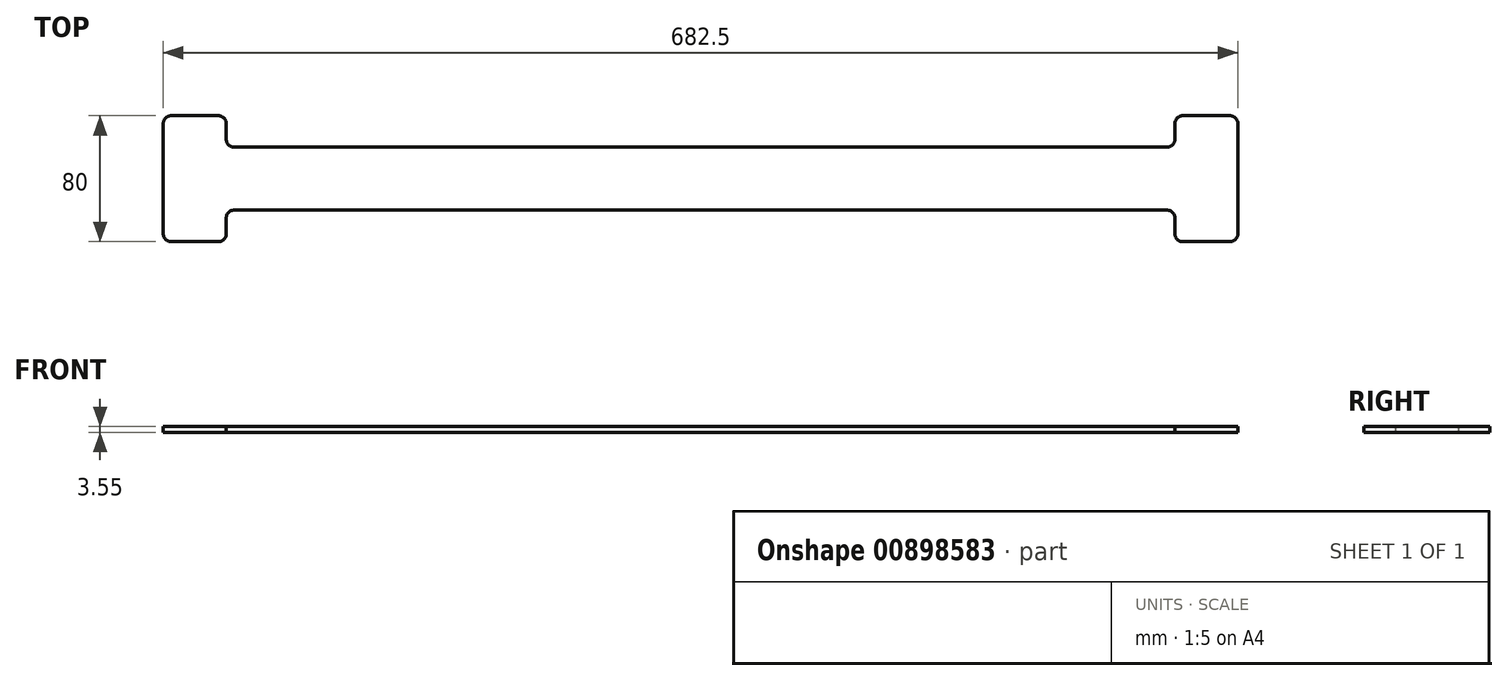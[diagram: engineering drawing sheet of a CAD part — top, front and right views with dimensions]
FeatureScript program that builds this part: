
annotation { "Feature Type Name" : "Feature", "Feature Type Description" : "" }
export const myFeature = defineFeature(function(context is Context, id is Id, definition is map)
    precondition{}
    {
        {
            var Q0;
            Q0=qCreatedBy(makeId("Top.planeOp"),FACE);
            var sketch = newSketch(context, id + "F0", { "sketchPlane" : qUnion([Q0])});
            skLineSegment(sketch, "E0.bottom", {"start": v(341.25, 20) * mm, "end": v(-341.25, 20) * mm});
            skLineSegment(sketch, "E0.top", {"start": v(341.25, -20) * mm, "end": v(-341.25, -20) * mm});
            skLineSegment(sketch, "E0.left", {"start": v(341.25, 20) * mm, "end": v(341.25, -20) * mm});
            skLineSegment(sketch, "E0.right", {"start": v(-341.25, 20) * mm, "end": v(-341.25, -20) * mm});
            skPoint(sketch, "E0.middle", {"position": v(0, 0) * mm});
            skLineSegment(sketch, "E1.bottom", {"start": v(-341.25, 0) * mm, "end": v(-301.25, 0) * mm, "construction": true});
            skLineSegment(sketch, "E1.top", {"start": v(-341.25, -40) * mm, "end": v(-301.25, -40) * mm});
            skLineSegment(sketch, "E1.left", {"start": v(-341.25, 0) * mm, "end": v(-341.25, -40) * mm});
            skLineSegment(sketch, "E1.right", {"start": v(-301.25, 0) * mm, "end": v(-301.25, -40) * mm});
            skLineSegment(sketch, "E2.bottom", {"start": v(341.25, 0) * mm, "end": v(301.25, 0) * mm, "construction": true});
            skLineSegment(sketch, "E2.top", {"start": v(341.25, -40) * mm, "end": v(301.25, -40) * mm});
            skLineSegment(sketch, "E2.left", {"start": v(341.25, 0) * mm, "end": v(341.25, -40) * mm});
            skLineSegment(sketch, "E2.right", {"start": v(301.25, 0) * mm, "end": v(301.25, -40) * mm});
            skLineSegment(sketch, "E3.MirrorCS", {"start": v(-341.25, 40) * mm, "end": v(-301.25, 40) * mm});
            skLineSegment(sketch, "E4.MirrorCS", {"start": v(-301.25, 0) * mm, "end": v(-301.25, 40) * mm});
            skLineSegment(sketch, "E5.MirrorCS", {"start": v(-341.25, 0) * mm, "end": v(-341.25, 40) * mm});
            skLineSegment(sketch, "E6.MirrorCS", {"start": v(301.25, 0) * mm, "end": v(301.25, 40) * mm});
            skLineSegment(sketch, "E7.MirrorCS", {"start": v(341.25, 40) * mm, "end": v(301.25, 40) * mm});
            skLineSegment(sketch, "E8.MirrorCS", {"start": v(341.25, 0) * mm, "end": v(341.25, 40) * mm});
            skSolve(sketch);
        }
        {
            var Q0;
            Q0 = qSketchRegion(id + "F0", true);
            extrude(context, id + "F1", {"entities" : qUnion([Q0]), "depth" : 3.55 * mm, "offsetDistance" : 25 * mm});
        }
        {
            var Q0;
            Q0=makeQuery(id+"F1.opExtrude","SWEPT_EDGE",EDGE,{"disambiguationData":[OSD([sQuery(id+"F0.wireOp",EDGE,"E0.bottom"),sQuery(id+"F0.wireOp",EDGE,"E4.MirrorCS")])]});
            var Q1;
            Q1=makeQuery(id+"F1.opExtrude","SWEPT_EDGE",EDGE,{"disambiguationData":[OSD([sQuery(id+"F0.wireOp",EDGE,"E3.MirrorCS"),sQuery(id+"F0.wireOp",EDGE,"E4.MirrorCS")])]});
            var Q2;
            Q2=makeQuery(id+"F1.opExtrude","SWEPT_EDGE",EDGE,{"disambiguationData":[OSD([sQuery(id+"F0.wireOp",EDGE,"E3.MirrorCS"),sQuery(id+"F0.wireOp",EDGE,"E5.MirrorCS")])]});
            var Q3;
            Q3=makeQuery(id+"F1.opExtrude","SWEPT_EDGE",EDGE,{"disambiguationData":[OSD([sQuery(id+"F0.wireOp",EDGE,"E1.top"),sQuery(id+"F0.wireOp",EDGE,"E1.right")])]});
            var Q4;
            Q4=makeQuery(id+"F1.opExtrude","SWEPT_EDGE",EDGE,{"disambiguationData":[OSD([sQuery(id+"F0.wireOp",EDGE,"E1.top"),sQuery(id+"F0.wireOp",EDGE,"E1.left")])]});
            var Q5;
            Q5=makeQuery(id+"F1.opExtrude","SWEPT_EDGE",EDGE,{"disambiguationData":[OSD([sQuery(id+"F0.wireOp",EDGE,"E0.top"),sQuery(id+"F0.wireOp",EDGE,"E1.right")])]});
            var Q6;
            Q6=makeQuery(id+"F1.opExtrude","SWEPT_EDGE",EDGE,{"disambiguationData":[OSD([sQuery(id+"F0.wireOp",EDGE,"E0.top"),sQuery(id+"F0.wireOp",EDGE,"E2.right")])]});
            var Q7;
            Q7=makeQuery(id+"F1.opExtrude","SWEPT_EDGE",EDGE,{"disambiguationData":[OSD([sQuery(id+"F0.wireOp",EDGE,"E2.top"),sQuery(id+"F0.wireOp",EDGE,"E2.right")])]});
            var Q8;
            Q8=makeQuery(id+"F1.opExtrude","SWEPT_EDGE",EDGE,{"disambiguationData":[OSD([sQuery(id+"F0.wireOp",EDGE,"E2.top"),sQuery(id+"F0.wireOp",EDGE,"E2.left")])]});
            var Q9;
            Q9=makeQuery(id+"F1.opExtrude","SWEPT_EDGE",EDGE,{"disambiguationData":[OSD([sQuery(id+"F0.wireOp",EDGE,"E7.MirrorCS"),sQuery(id+"F0.wireOp",EDGE,"E8.MirrorCS")])]});
            var Q10;
            Q10=makeQuery(id+"F1.opExtrude","SWEPT_EDGE",EDGE,{"disambiguationData":[OSD([sQuery(id+"F0.wireOp",EDGE,"E6.MirrorCS"),sQuery(id+"F0.wireOp",EDGE,"E7.MirrorCS")])]});
            var Q11;
            Q11=makeQuery(id+"F1.opExtrude","SWEPT_EDGE",EDGE,{"disambiguationData":[OSD([sQuery(id+"F0.wireOp",EDGE,"E0.bottom"),sQuery(id+"F0.wireOp",EDGE,"E6.MirrorCS")])]});
            fillet(context, id + "F2", {"entities" : qUnion([Q0, Q1, Q2, Q3, Q4, Q5, Q6, Q7, Q8, Q9, Q10, Q11]), "radius" : 5 * mm, "tangentPropagation" : true, "allowEdgeOverflow" : false});
        }
    });
